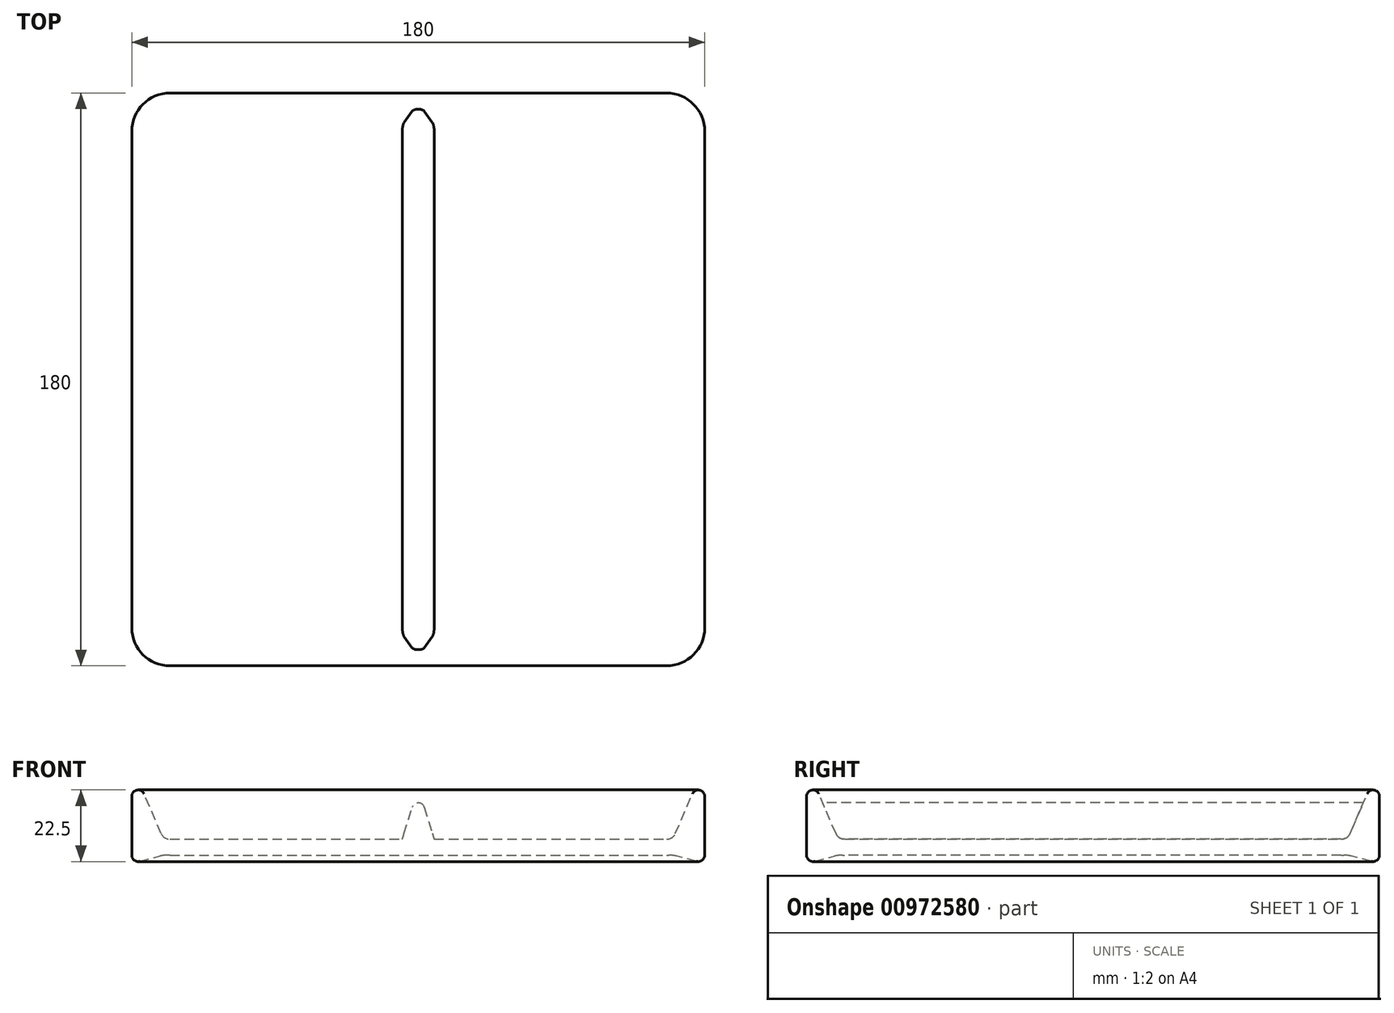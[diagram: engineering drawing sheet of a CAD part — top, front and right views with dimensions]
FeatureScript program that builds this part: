
annotation { "Feature Type Name" : "Feature", "Feature Type Description" : "" }
export const myFeature = defineFeature(function(context is Context, id is Id, definition is map)
    precondition{}
    {
        {
            var Q0;
            Q0=qCreatedBy(makeId("Top.planeOp"),FACE);
            var sketch = newSketch(context, id + "F0", { "sketchPlane" : qUnion([Q0])});
            skLineSegment(sketch, "E0.bottom", {"start": v(-78, 90) * mm, "end": v(78, 90) * mm});
            skLineSegment(sketch, "E0.top", {"start": v(-78, -90) * mm, "end": v(78, -90) * mm});
            skLineSegment(sketch, "E0.left", {"start": v(-90, 78) * mm, "end": v(-90, -78) * mm});
            skLineSegment(sketch, "E0.right", {"start": v(90, 78) * mm, "end": v(90, -78) * mm});
            skPoint(sketch, "E0.middle", {"position": v(0, 0) * mm});
            skPoint(sketch, "E1.visualSharp", {"position": v(-90, 90) * mm});
            skArc(sketch, "E1.filletArc", {"start": v(-78, 90) * mm, "mid": v(-86.49, 86.49) * mm, "end": v(-90, 78) * mm});
            skPoint(sketch, "E2.visualSharp", {"position": v(-90, -90) * mm});
            skArc(sketch, "E2.filletArc", {"start": v(-90, -78) * mm, "mid": v(-86.49, -86.49) * mm, "end": v(-78, -90) * mm});
            skPoint(sketch, "E3.visualSharp", {"position": v(90, -90) * mm});
            skArc(sketch, "E3.filletArc", {"start": v(78, -90) * mm, "mid": v(86.49, -86.49) * mm, "end": v(90, -78) * mm});
            skPoint(sketch, "E4.visualSharp", {"position": v(90, 90) * mm});
            skArc(sketch, "E4.filletArc", {"start": v(90, 78) * mm, "mid": v(86.49, 86.49) * mm, "end": v(78, 90) * mm});
            skSolve(sketch);
        }
        {
            var Q0;
            Q0=qCreatedBy(makeId("Right.planeOp"),FACE);
            var sketch = newSketch(context, id + "F1", { "sketchPlane" : qUnion([Q0])});
            skLineSegment(sketch, "E5.bottom", {"start": v(-79, 20.5) * mm, "end": v(-90, 20.5) * mm, "construction": true});
            skLineSegment(sketch, "E5.top", {"start": v(-79, -2) * mm, "end": v(-90, -2) * mm, "construction": true});
            skLineSegment(sketch, "E5.left", {"start": v(-79, 20.5) * mm, "end": v(-79, -2) * mm, "construction": true});
            skLineSegment(sketch, "E5.right", {"start": v(-90, 20.5) * mm, "end": v(-90, -2) * mm, "construction": true});
            skLineSegment(sketch, "E6", {"start": v(-90, 18.5) * mm, "end": v(-90, 0) * mm});
            skLineSegment(sketch, "E7", {"start": v(-87.5, -1.94) * mm, "end": v(-80, 0) * mm});
            skLineSegment(sketch, "E8", {"start": v(-80, 0) * mm, "end": v(-79, 0) * mm});
            skLineSegment(sketch, "E9", {"start": v(-79, 0) * mm, "end": v(-79, 5) * mm});
            skLineSegment(sketch, "E10", {"start": v(-79, 5) * mm, "end": v(-80, 5) * mm});
            skLineSegment(sketch, "E11", {"start": v(-80, 5) * mm, "end": v(-86.16, 19.3) * mm});
            skPoint(sketch, "E12.visualSharp", {"position": v(-90, 28.19) * mm});
            skArc(sketch, "E12.filletArc", {"start": v(-86.16, 19.3) * mm, "mid": v(-88.4, 20.46) * mm, "end": v(-90, 18.5) * mm});
            skPoint(sketch, "E13.visualSharp", {"position": v(-90, -2.58) * mm});
            skArc(sketch, "E13.filletArc", {"start": v(-90, 0) * mm, "mid": v(-89.22, -1.58) * mm, "end": v(-87.5, -1.94) * mm});
            skSolve(sketch);
        }
        {
            var Q0;
            Q0=makeQuery(id+"F1.imprint","IMPRINT",FACE,{"disambiguationData":[TD([[makeQuery(id+"F1.imprint","IMPRINT",EDGE,{"derivedFrom":sQuery(id+"F1.wireOp",EDGE,"E6")}),1.0]])]});
            var Q1;
            Q1=qConstructionFilter(qBodyType(qCreatedBy(id+"F0",EDGE),BodyType.WIRE),ConstructionObject.NO);
            sweep(context, id + "F2", {"profiles" : qUnion([Q0]), "path" : qUnion([Q1])});
        }
        {
            var Q0;
            Q0=makeQuery(id+"F2.opSweep","SWEPT_FACE",FACE,{"disambiguationData":[OSD([sQuery(id+"F0.wireOp",EDGE,"E0.top"),sQuery(id+"F1.wireOp",EDGE,"E10")])]});
            var sketch = newSketch(context, id + "F3", { "sketchPlane" : qUnion([Q0])});
            skLineSegment(sketch, "E14.0", {"start": v(78, 79) * mm, "end": v(-78, 79) * mm});
            skPoint(sketch, "E15.0", {"position": v(-78.7, 78.7) * mm});
            skArc(sketch, "E16.0", {"start": v(-78, 79) * mm, "mid": v(-78.7, 78.7) * mm, "end": v(-79, 78) * mm});
            skLineSegment(sketch, "E17.0", {"start": v(-79, 78) * mm, "end": v(-79, -78) * mm});
            skArc(sketch, "E18.0", {"start": v(-79, -78) * mm, "mid": v(-78.7, -78.7) * mm, "end": v(-78, -79) * mm});
            skLineSegment(sketch, "E19.0", {"start": v(-78, -79) * mm, "end": v(78, -79) * mm});
            skArc(sketch, "E20.0", {"start": v(78, -79) * mm, "mid": v(78.7, -78.7) * mm, "end": v(79, -78) * mm});
            skLineSegment(sketch, "E21.0", {"start": v(79, -78) * mm, "end": v(79, 78) * mm});
            skArc(sketch, "E22.0", {"start": v(79, 78) * mm, "mid": v(78.7, 78.7) * mm, "end": v(78, 79) * mm});
            skSolve(sketch);
        }
        {
            var Q0;
            Q0=qSketchRegion(id+"F3",true);
            var Q1;
            Q1=makeQuery(id+"F2.opSweep","SWEPT_FACE",FACE,{"disambiguationData":[OSD([sQuery(id+"F0.wireOp",EDGE,"E0.top"),sQuery(id+"F1.wireOp",EDGE,"E8")])]});
            extrude(context, id + "F4", {"entities" : qUnion([Q0]), "operationType" : NewBodyOperationType.ADD, "endBound" : BoundingType.UP_TO_SURFACE, "oppositeDirection" : true, "depth" : 25 * mm, "endBoundEntityFace" : qUnion([Q1]), "offsetDistance" : 25 * mm});
        }
        {
            var Q0;
            Q0=makeQuery(id+"F4.boolean.opBoolean","MERGE",FACE,{"derivedFrom":[makeQuery(id+"F2.opSweep","SWEPT_FACE",FACE,{"disambiguationData":[OSD([sQuery(id+"F0.wireOp",EDGE,"E0.top"),sQuery(id+"F1.wireOp",EDGE,"E10")])]}),makeQuery(id+"F4.opExtrude","CAP_FACE",FACE,{"disambiguationData":[OSD([sQuery(id+"F3.wireOp",EDGE,"E14.0"),sQuery(id+"F3.wireOp",EDGE,"E16.0"),sQuery(id+"F3.wireOp",EDGE,"E17.0"),sQuery(id+"F3.wireOp",EDGE,"E18.0"),sQuery(id+"F3.wireOp",EDGE,"E19.0"),sQuery(id+"F3.wireOp",EDGE,"E20.0"),sQuery(id+"F3.wireOp",EDGE,"E21.0"),sQuery(id+"F3.wireOp",EDGE,"E22.0")])],"isStart":true})]});
            var sketch = newSketch(context, id + "F5", { "sketchPlane" : qUnion([Q0])});
            skLineSegment(sketch, "E23", {"start": v(-90, 0) * mm, "end": v(90, 0) * mm, "construction": true});
            skLineSegment(sketch, "E24", {"start": v(0, 90) * mm, "end": v(0, 0) * mm, "construction": true});
            skSolve(sketch);
        }
        {
            var Q0;
            Q0=qCreatedBy(makeId("Front.planeOp"),FACE);
            var sketch = newSketch(context, id + "F6", { "sketchPlane" : qUnion([Q0])});
            skLineSegment(sketch, "E25", {"start": v(-5, 5) * mm, "end": v(5, 5) * mm});
            skLineSegment(sketch, "E26", {"start": v(5, 5) * mm, "end": v(1.91, 15.05) * mm});
            skLineSegment(sketch, "E27", {"start": v(-1.91, 15.05) * mm, "end": v(-5, 5) * mm});
            skPoint(sketch, "E28.visualSharp", {"position": v(0, 21.27) * mm});
            skArc(sketch, "E28.filletArc", {"start": v(1.91, 15.05) * mm, "mid": v(0, 16.46) * mm, "end": v(-1.91, 15.05) * mm});
            skLineSegment(sketch, "E29", {"start": v(-65.02, 16.46) * mm, "end": v(-27.84, 16.46) * mm, "construction": true});
            skSolve(sketch);
        }
        {
            var Q0;
            Q0=qSketchRegion(id+"F6",true);
            var Q1;
            Q1=makeQuery(id+"F2.opSweep","SWEPT_FACE",FACE,{"disambiguationData":[OSD([sQuery(id+"F0.wireOp",EDGE,"E0.bottom"),sQuery(id+"F1.wireOp",EDGE,"E11")])]});
            var Q2;
            Q2=makeQuery(id+"F2.opSweep","SWEPT_FACE",FACE,{"disambiguationData":[OSD([sQuery(id+"F0.wireOp",EDGE,"E0.top"),sQuery(id+"F1.wireOp",EDGE,"E11")])]});
            extrude(context, id + "F7", {"entities" : qUnion([Q0]), "operationType" : NewBodyOperationType.ADD, "endBound" : BoundingType.UP_TO_SURFACE, "oppositeDirection" : true, "depth" : 25 * mm, "endBoundEntityFace" : qUnion([Q1]), "offsetDistance" : 25 * mm, "hasSecondDirection" : true, "secondDirectionBound" : SecondDirectionBoundingType.UP_TO_SURFACE, "secondDirectionOppositeDirection" : false, "secondDirectionDepth" : 25 * mm, "secondDirectionBoundEntityFace" : qUnion([Q2])});
        }
        {
            var Q0;
            {var subQ0=sQuery(id+"F1.wireOp",EDGE,"E11");var subQ1=sQuery(id+"F1.wireOp",EDGE,"E10");var subQ2=sQuery(id+"F0.wireOp",EDGE,"E0.bottom");Q0=makeQuery(id+"F7.boolean.opBoolean","SPLIT",EDGE,{"disambiguationData":[TD([makeQuery(id+"F7.opExtrude","SWEPT_FACE",FACE,{"disambiguationData":[OSD([sQuery(id+"F6.wireOp",EDGE,"E27")])]})])],"derivedFrom":makeQuery(id+"F2.opSweep","SWEPT_EDGE",EDGE,{"disambiguationData":[OSD([subQ2,subQ1,subQ0])]})});}
            var Q1;
            {var subQ0=sQuery(id+"F1.wireOp",EDGE,"E11");var subQ1=sQuery(id+"F0.wireOp",EDGE,"E0.bottom");var subQ2=sQuery(id+"F1.wireOp",EDGE,"E10");Q1=makeQuery(id+"F7.boolean.opBoolean","SPLIT",EDGE,{"disambiguationData":[TD([makeQuery(id+"F7.opExtrude","SWEPT_FACE",FACE,{"disambiguationData":[OSD([sQuery(id+"F6.wireOp",EDGE,"E26")])]})])],"derivedFrom":makeQuery(id+"F2.opSweep","SWEPT_EDGE",EDGE,{"disambiguationData":[OSD([subQ1,subQ2,subQ0])]})});}
            var Q2;
            Q2=makeQuery(id+"F7.opExtrude","TWEAK_EDGE",EDGE,{"derivedFrom":[makeQuery(id+"F6.imprint","IMPRINT",EDGE,{"derivedFrom":sQuery(id+"F6.wireOp",EDGE,"E25")}),makeQuery(id+"F6.imprint","IMPRINT",EDGE,{"derivedFrom":sQuery(id+"F6.wireOp",EDGE,"E26")})]});
            var Q3;
            Q3=makeQuery(id+"F7.opExtrude","TWEAK_EDGE",EDGE,{"derivedFrom":[makeQuery(id+"F6.imprint","IMPRINT",EDGE,{"derivedFrom":sQuery(id+"F6.wireOp",EDGE,"E25")}),makeQuery(id+"F6.imprint","IMPRINT",EDGE,{"derivedFrom":sQuery(id+"F6.wireOp",EDGE,"E27")})]});
            var Q4;
            Q4=makeQuery(id+"F7.opExtrude","CAP_EDGE",EDGE,{"disambiguationData":[OSD([sQuery(id+"F6.wireOp",EDGE,"E27")]),topologyDisambiguationEdgeConnected([makeQuery(id+"F2.opSweep","SWEPT_FACE",FACE,{"disambiguationData":[OSD([sQuery(id+"F0.wireOp",EDGE,"E0.bottom"),sQuery(id+"F1.wireOp",EDGE,"E11")])]})])],"isStart":false});
            var Q5;
            Q5=makeQuery(id+"F7.opExtrude","CAP_EDGE",EDGE,{"disambiguationData":[OSD([sQuery(id+"F6.wireOp",EDGE,"E26")]),topologyDisambiguationEdgeConnected([makeQuery(id+"F2.opSweep","SWEPT_FACE",FACE,{"disambiguationData":[OSD([sQuery(id+"F0.wireOp",EDGE,"E0.top"),sQuery(id+"F1.wireOp",EDGE,"E11")])]})])],"isStart":false});
            fillet(context, id + "F8", {"entities" : qUnion([Q0, Q1, Q2, Q3, Q4, Q5]), "radius" : 3 * mm, "tangentPropagation" : true, "allowEdgeOverflow" : false});
        }
        {
            var Q0;
            Q0=makeQuery(id+"F2.opSweep","SWEPT_EDGE",EDGE,{"disambiguationData":[OSD([sQuery(id+"F0.wireOp",EDGE,"E0.top"),sQuery(id+"F1.wireOp",EDGE,"E7"),sQuery(id+"F1.wireOp",EDGE,"E8")])]});
            fillet(context, id + "F9", {"entities" : qUnion([Q0]), "radius" : 10 * mm, "tangentPropagation" : true, "allowEdgeOverflow" : false});
        }
    });
